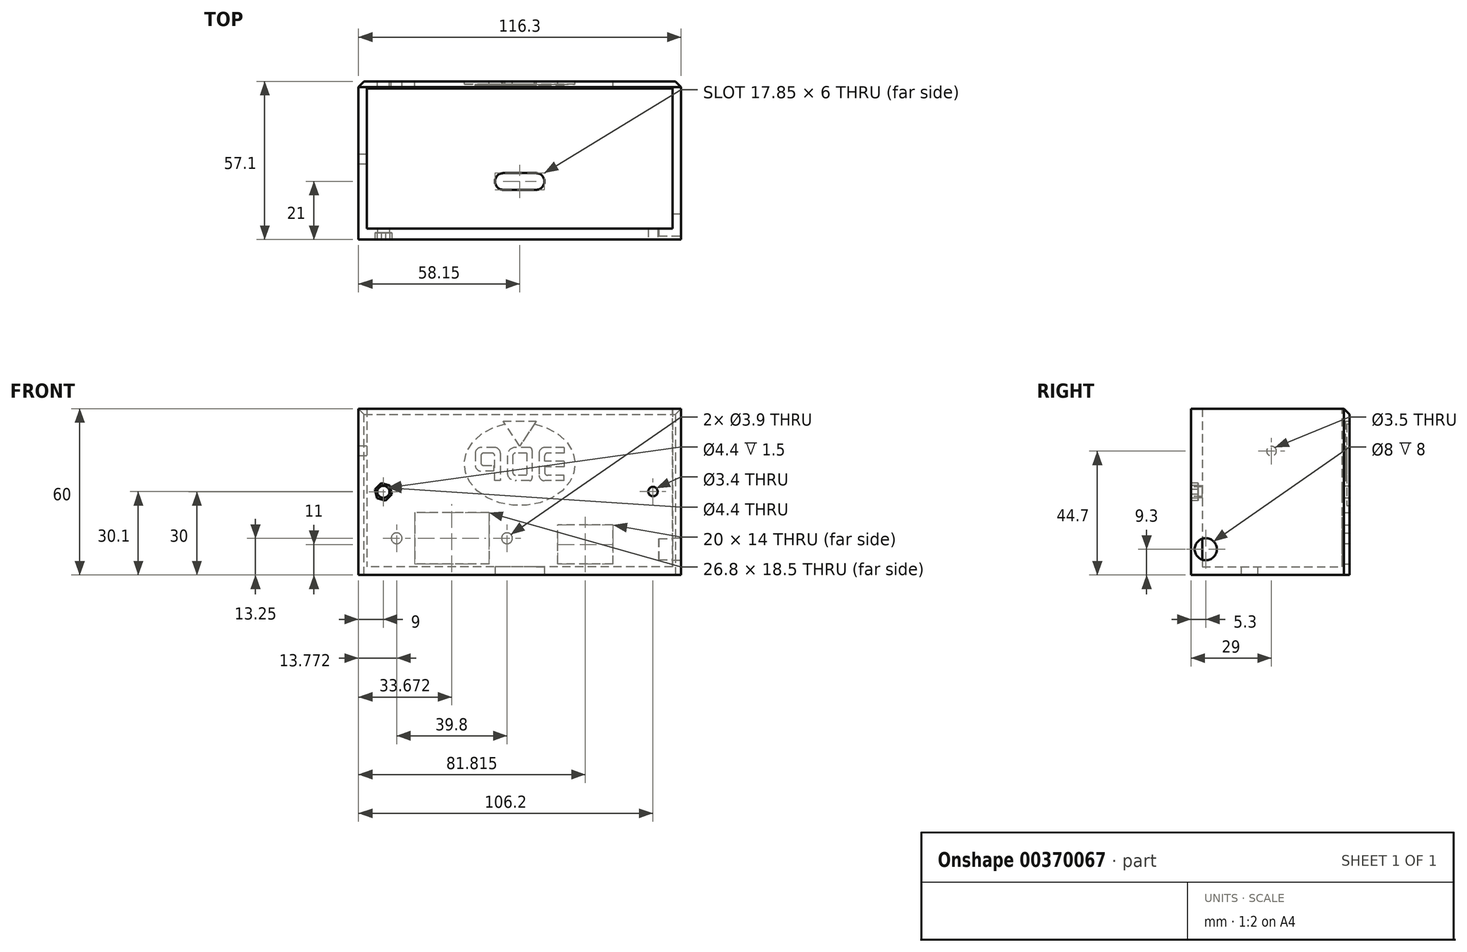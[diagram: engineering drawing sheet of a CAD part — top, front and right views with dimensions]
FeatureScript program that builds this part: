
annotation { "Feature Type Name" : "Feature", "Feature Type Description" : "" }
export const myFeature = defineFeature(function(context is Context, id is Id, definition is map)
    precondition{}
    {
        {
            var Q0;
            Q0=qCreatedBy(makeId("Front.planeOp"),FACE);
            var sketch = newSketch(context, id + "F0", { "sketchPlane" : qUnion([Q0])});
            skLineSegment(sketch, "E0.bottom", {"start": v(0, 0) * mm, "end": v(116.3, 0) * mm});
            skLineSegment(sketch, "E0.top", {"start": v(0, 70) * mm, "end": v(116.3, 70) * mm});
            skLineSegment(sketch, "E0.left", {"start": v(0, 0) * mm, "end": v(0, 70) * mm});
            skLineSegment(sketch, "E0.right", {"start": v(116.3, 0) * mm, "end": v(116.3, 70) * mm});
            skCircle(sketch, "E1", {"center": v(18, 61.5) * mm, "radius": 1.7 * mm});
            skCircle(sketch, "E2", {"center": v(103.3, 61.5) * mm, "radius": 1.7 * mm});
            skCircle(sketch, "E3", {"center": v(106.2, 5.1) * mm, "radius": 1.7 * mm});
            skCircle(sketch, "E4", {"center": v(9, 5) * mm, "radius": 2.2 * mm});
            skLineSegment(sketch, "E5.top", {"start": v(116.3, 0) * mm, "end": v(119.3, 0) * mm});
            skPoint(sketch, "E6.orphan", {"position": v(-3, 70) * mm});
            skPoint(sketch, "E7.right.end.orphan", {"position": v(-3, 35) * mm});
            skPoint(sketch, "E8.right.end.orphan", {"position": v(119.3, 35) * mm});
            skPoint(sketch, "E5.bottom.end.orphan", {"position": v(119.3, 70) * mm});
            skPoint(sketch, "E9.top.end.orphan", {"position": v(-3, 0) * mm});
            skSolve(sketch);
        }
        {
            var Q0;
            Q0=makeQuery(id+"F0.imprint","IMPRINT",FACE,{"disambiguationData":[TD([[makeQuery(id+"F0.imprint","IMPRINT",EDGE,{"derivedFrom":sQuery(id+"F0.wireOp",EDGE,"E0.bottom")}),1.0]])]});
            extrude(context, id + "F1", {"entities" : qUnion([Q0]), "oppositeDirection" : true, "depth" : 4 * mm});
        }
        {
            var Q0;
            Q0=makeQuery(id+"F1.opExtrude","CAP_FACE",FACE,{"disambiguationData":[OSD([sQuery(id+"F0.wireOp",EDGE,"E0.bottom"),sQuery(id+"F0.wireOp",EDGE,"E0.top"),sQuery(id+"F0.wireOp",EDGE,"E0.left"),sQuery(id+"F0.wireOp",EDGE,"E0.right"),sQuery(id+"F0.wireOp",EDGE,"E1"),sQuery(id+"F0.wireOp",EDGE,"E2"),sQuery(id+"F0.wireOp",EDGE,"E3"),sQuery(id+"F0.wireOp",EDGE,"E4")])],"isStart":false});
            var sketch = newSketch(context, id + "F2", { "sketchPlane" : qUnion([Q0])});
            skPoint(sketch, "E10.oppositeSnap0", {"position": v(-116.3, 35) * mm});
            skLineSegment(sketch, "E10.top", {"start": v(-116.3, 35) * mm, "end": v(-113.3, 35) * mm});
            skLineSegment(sketch, "E10.left", {"start": v(-116.3, 0) * mm, "end": v(-116.3, 35) * mm});
            skLineSegment(sketch, "E10.right", {"start": v(-113.3, 0) * mm, "end": v(-113.3, 35) * mm});
            skPoint(sketch, "E11.oppositeSnap0", {"position": v(0, 35) * mm});
            skLineSegment(sketch, "E11.top", {"start": v(0, 35) * mm, "end": v(-3, 35) * mm});
            skLineSegment(sketch, "E11.left", {"start": v(0, 0) * mm, "end": v(0, 35) * mm});
            skLineSegment(sketch, "E11.right", {"start": v(-3, 0) * mm, "end": v(-3, 35) * mm});
            skLineSegment(sketch, "E12.top", {"start": v(-116.3, -25) * mm, "end": v(-113.3, -25) * mm});
            skLineSegment(sketch, "E12.left", {"start": v(-116.3, 0) * mm, "end": v(-116.3, -25) * mm});
            skLineSegment(sketch, "E12.right", {"start": v(-113.3, 0) * mm, "end": v(-113.3, -25) * mm});
            skLineSegment(sketch, "E13.top", {"start": v(0, -25) * mm, "end": v(-3, -25) * mm});
            skLineSegment(sketch, "E13.left", {"start": v(0, 0) * mm, "end": v(0, -25) * mm});
            skLineSegment(sketch, "E13.right", {"start": v(-3, 0) * mm, "end": v(-3, -25) * mm});
            skSolve(sketch);
        }
        {
            var Q0;
            Q0 = qSketchRegion(id + "F2", true);
            extrude(context, id + "F3", {"entities" : qUnion([Q0]), "operationType" : NewBodyOperationType.ADD, "depth" : 53.1 * mm});
        }
        {
            var Q0;
            Q0=makeQuery(id+"F3.boolean.opBoolean","MERGE",FACE,{"derivedFrom":[makeQuery(id+"F1.opExtrude","SWEPT_FACE",FACE,{"disambiguationData":[OSD([sQuery(id+"F0.wireOp",EDGE,"E0.left")])]}),makeQuery(id+"F3.opExtrude","SWEPT_FACE",FACE,{"disambiguationData":[OSD([sQuery(id+"F2.wireOp",EDGE,"E11.left"),sQuery(id+"F2.wireOp",EDGE,"E13.left")])]})]});
            var sketch = newSketch(context, id + "F4", { "sketchPlane" : qUnion([Q0])});
            skLineSegment(sketch, "E14", {"start": v(-57.1, 35) * mm, "end": v(-57.1, -25) * mm});
            skLineSegment(sketch, "E15", {"start": v(-57.1, -25) * mm, "end": v(0, -25) * mm});
            skLineSegment(sketch, "E16", {"start": v(0, -25) * mm, "end": v(0, 0) * mm});
            skLineSegment(sketch, "E17", {"start": v(0, 0) * mm, "end": v(-4, 0) * mm});
            skLineSegment(sketch, "E18", {"start": v(-4, 0) * mm, "end": v(-4, -22) * mm});
            skLineSegment(sketch, "E19", {"start": v(-4, -22) * mm, "end": v(-54.5, -22) * mm});
            skLineSegment(sketch, "E20", {"start": v(-54.5, -22) * mm, "end": v(-54.5, 35) * mm});
            skLineSegment(sketch, "E21", {"start": v(-54.5, 35) * mm, "end": v(-57.1, 35) * mm});
            skSolve(sketch);
        }
        {
            var Q0;
            Q0 = qSketchRegion(id + "F4", true);
            extrude(context, id + "F5", {"entities" : qUnion([Q0]), "operationType" : NewBodyOperationType.ADD, "oppositeDirection" : true, "depth" : 116.3 * mm});
        }
        {
            var Q0;
            Q0=makeQuery(id+"F5.boolean.opBoolean","MERGE",FACE,{"derivedFrom":[makeQuery(id+"F3.opExtrude","CAP_FACE",FACE,{"disambiguationData":[OSD([sQuery(id+"F2.wireOp",EDGE,"E10.top"),sQuery(id+"F2.wireOp",EDGE,"E10.left"),sQuery(id+"F2.wireOp",EDGE,"E10.right"),sQuery(id+"F2.wireOp",EDGE,"E12.top"),sQuery(id+"F2.wireOp",EDGE,"E12.left"),sQuery(id+"F2.wireOp",EDGE,"E12.right")])],"isStart":false}),makeQuery(id+"F3.opExtrude","CAP_FACE",FACE,{"disambiguationData":[OSD([sQuery(id+"F2.wireOp",EDGE,"E11.top"),sQuery(id+"F2.wireOp",EDGE,"E11.left"),sQuery(id+"F2.wireOp",EDGE,"E11.right"),sQuery(id+"F2.wireOp",EDGE,"E13.top"),sQuery(id+"F2.wireOp",EDGE,"E13.left"),sQuery(id+"F2.wireOp",EDGE,"E13.right")])],"isStart":false}),makeQuery(id+"F5.opExtrude","SWEPT_FACE",FACE,{"disambiguationData":[OSD([sQuery(id+"F4.wireOp",EDGE,"E14")])]})]});
            var sketch = newSketch(context, id + "F6", { "sketchPlane" : qUnion([Q0])});
            skLineSegment(sketch, "E22.bottom", {"start": v(-47.07, -2.5) * mm, "end": v(-20.27, -2.5) * mm});
            skLineSegment(sketch, "E22.top", {"start": v(-47.07, -21) * mm, "end": v(-20.27, -21) * mm});
            skLineSegment(sketch, "E22.left", {"start": v(-47.07, -2.5) * mm, "end": v(-47.07, -21) * mm});
            skLineSegment(sketch, "E22.right", {"start": v(-20.27, -2.5) * mm, "end": v(-20.27, -21) * mm});
            skPoint(sketch, "E23.right.end.orphan", {"position": v(-79.44, -21) * mm});
            skLineSegment(sketch, "E24", {"start": v(-20.27, -11.75) * mm, "end": v(-13.77, -11.75) * mm});
            skCircle(sketch, "E25", {"center": v(-13.77, -11.75) * mm, "radius": 1.95 * mm});
            skLineSegment(sketch, "E26", {"start": v(-33.67, -2.5) * mm, "end": v(-33.67, -21) * mm, "construction": true});
            skCircle(sketch, "E27.MirrorC", {"center": v(-53.57, -11.75) * mm, "radius": 1.95 * mm});
            skLineSegment(sketch, "E28.bottom", {"start": v(-91.81, -21) * mm, "end": v(-71.81, -21) * mm});
            skLineSegment(sketch, "E28.top", {"start": v(-91.81, -7) * mm, "end": v(-71.81, -7) * mm});
            skLineSegment(sketch, "E28.left", {"start": v(-91.81, -21) * mm, "end": v(-91.81, -7) * mm});
            skLineSegment(sketch, "E28.right", {"start": v(-71.81, -21) * mm, "end": v(-71.81, -7) * mm});
            skSolve(sketch);
        }
        {
            var Q0;
            Q0 = qSketchRegion(id + "F6", true);
            extrude(context, id + "F7", {"entities" : qUnion([Q0]), "operationType" : NewBodyOperationType.REMOVE, "oppositeDirection" : true, "depth" : 25 * mm});
        }
        {
            var Q0;
            Q0=makeQuery(id+"F5.boolean.opBoolean","MERGE",FACE,{"derivedFrom":[makeQuery(id+"F3.boolean.opBoolean","MERGE",FACE,{"derivedFrom":[makeQuery(id+"F1.opExtrude","SWEPT_FACE",FACE,{"disambiguationData":[OSD([sQuery(id+"F0.wireOp",EDGE,"E0.left")])]}),makeQuery(id+"F3.opExtrude","SWEPT_FACE",FACE,{"disambiguationData":[OSD([sQuery(id+"F2.wireOp",EDGE,"E11.left"),sQuery(id+"F2.wireOp",EDGE,"E13.left")])]})]}),makeQuery(id+"F5.opExtrude","CAP_FACE",FACE,{"disambiguationData":[OSD([sQuery(id+"F4.wireOp",EDGE,"E14"),sQuery(id+"F4.wireOp",EDGE,"E15"),sQuery(id+"F4.wireOp",EDGE,"E16"),sQuery(id+"F4.wireOp",EDGE,"E17"),sQuery(id+"F4.wireOp",EDGE,"E18"),sQuery(id+"F4.wireOp",EDGE,"E19"),sQuery(id+"F4.wireOp",EDGE,"E20"),sQuery(id+"F4.wireOp",EDGE,"E21")])],"isStart":true})]});
            var sketch = newSketch(context, id + "F8", { "sketchPlane" : qUnion([Q0])});
            skLineSegment(sketch, "E29", {"start": v(0, 0) * mm, "end": v(-29, 0) * mm, "construction": true});
            skLineSegment(sketch, "E30", {"start": v(-29, 0) * mm, "end": v(-29, 19.7) * mm, "construction": true});
            skCircle(sketch, "E31", {"center": v(-29, 19.7) * mm, "radius": 1.75 * mm});
            skLineSegment(sketch, "E32", {"start": v(-4, 70) * mm, "end": v(0, 70) * mm});
            skSolve(sketch);
        }
        {
            var Q0;
            Q0=makeQuery(id+"F8.imprint","IMPRINT",FACE,{"disambiguationData":[TD([[makeQuery(id+"F8.imprint","IMPRINT",EDGE,{"derivedFrom":sQuery(id+"F8.wireOp",EDGE,"E31")}),1.0]])]});
            extrude(context, id + "F9", {"entities" : qUnion([Q0]), "operationType" : NewBodyOperationType.REMOVE, "oppositeDirection" : true, "depth" : 25 * mm});
        }
        {
            var Q0;
            Q0=makeQuery(id+"F5.boolean.opBoolean","MERGE",FACE,{"derivedFrom":[makeQuery(id+"F1.opExtrude","CAP_FACE",FACE,{"disambiguationData":[OSD([sQuery(id+"F0.wireOp",EDGE,"E0.bottom"),sQuery(id+"F0.wireOp",EDGE,"E0.top"),sQuery(id+"F0.wireOp",EDGE,"E0.left"),sQuery(id+"F0.wireOp",EDGE,"E0.right"),sQuery(id+"F0.wireOp",EDGE,"E1"),sQuery(id+"F0.wireOp",EDGE,"E2"),sQuery(id+"F0.wireOp",EDGE,"E3"),sQuery(id+"F0.wireOp",EDGE,"E4")])],"isStart":false}),makeQuery(id+"F5.opExtrude","SWEPT_FACE",FACE,{"disambiguationData":[OSD([sQuery(id+"F4.wireOp",EDGE,"E18")])]})]});
            var sketch = newSketch(context, id + "F10", { "sketchPlane" : qUnion([Q0])});
            skLineSegment(sketch, "E33.bottom", {"start": v(-116.3, 70) * mm, "end": v(0, 70) * mm});
            skLineSegment(sketch, "E33.top", {"start": v(-116.3, 35) * mm, "end": v(0, 35) * mm});
            skLineSegment(sketch, "E33.left", {"start": v(-116.3, 70) * mm, "end": v(-116.3, 35) * mm});
            skLineSegment(sketch, "E33.right", {"start": v(0, 70) * mm, "end": v(0, 35) * mm});
            skSolve(sketch);
        }
        {
            var Q0;
            Q0 = qSketchRegion(id + "F10", true);
            extrude(context, id + "F11", {"entities" : qUnion([Q0]), "operationType" : NewBodyOperationType.REMOVE, "oppositeDirection" : true, "depth" : 25 * mm});
        }
        {
            var Q0;
            Q0=makeQuery(id+"F5.boolean.opBoolean","MERGE",FACE,{"derivedFrom":[makeQuery(id+"F3.opExtrude","CAP_FACE",FACE,{"disambiguationData":[OSD([sQuery(id+"F2.wireOp",EDGE,"E10.top"),sQuery(id+"F2.wireOp",EDGE,"E10.left"),sQuery(id+"F2.wireOp",EDGE,"E10.right"),sQuery(id+"F2.wireOp",EDGE,"E12.top"),sQuery(id+"F2.wireOp",EDGE,"E12.left"),sQuery(id+"F2.wireOp",EDGE,"E12.right")])],"isStart":false}),makeQuery(id+"F3.opExtrude","CAP_FACE",FACE,{"disambiguationData":[OSD([sQuery(id+"F2.wireOp",EDGE,"E11.top"),sQuery(id+"F2.wireOp",EDGE,"E11.left"),sQuery(id+"F2.wireOp",EDGE,"E11.right"),sQuery(id+"F2.wireOp",EDGE,"E13.top"),sQuery(id+"F2.wireOp",EDGE,"E13.left"),sQuery(id+"F2.wireOp",EDGE,"E13.right")])],"isStart":false}),makeQuery(id+"F5.opExtrude","SWEPT_FACE",FACE,{"disambiguationData":[OSD([sQuery(id+"F4.wireOp",EDGE,"E14")])]})]});
            var sketch = newSketch(context, id + "F12", { "sketchPlane" : qUnion([Q0])});
            skLineSegment(sketch, "E34", {"start": v(-78.15, 15) * mm, "end": v(-38.15, 15) * mm, "construction": true});
            skEllipticalArc(sketch, "E35", {});
            skPoint(sketch, "E36.orphan", {"position": v(-78.15, 30) * mm});
            skPoint(sketch, "E37.orphan", {"position": v(-38.15, 30) * mm});
            skPoint(sketch, "E38.orphan", {"position": v(-38.15, 0) * mm});
            skPoint(sketch, "E39.top.start.orphan", {"position": v(-78.15, 0) * mm});
            skLineSegment(sketch, "E40.bottom", {"start": v(-74.15, 21) * mm, "end": v(-67.15, 21) * mm});
            skLineSegment(sketch, "E40.top", {"start": v(-74.15, 9) * mm, "end": v(-67.15, 9) * mm});
            skLineSegment(sketch, "E40.right", {"start": v(-65.15, 19) * mm, "end": v(-65.15, 11) * mm});
            skLineSegment(sketch, "E41.bottom", {"start": v(-61.65, 21) * mm, "end": v(-56.65, 21) * mm});
            skLineSegment(sketch, "E41.top", {"start": v(-61.65, 9) * mm, "end": v(-56.65, 9) * mm});
            skLineSegment(sketch, "E41.left", {"start": v(-62.65, 20) * mm, "end": v(-62.65, 10) * mm});
            skLineSegment(sketch, "E41.right", {"start": v(-53.65, 18) * mm, "end": v(-53.65, 12) * mm});
            skLineSegment(sketch, "E42.bottom", {"start": v(-49.15, 21) * mm, "end": v(-44.15, 21) * mm});
            skLineSegment(sketch, "E42.left", {"start": v(-51.15, 19) * mm, "end": v(-51.15, 9) * mm});
            skLineSegment(sketch, "E42.right", {"start": v(-42.15, 19) * mm, "end": v(-42.15, 14.5) * mm});
            skPoint(sketch, "E43.visualSharp", {"position": v(-65.15, 21) * mm});
            skArc(sketch, "E43.filletArc", {"start": v(-65.15, 19) * mm, "mid": v(-65.74, 20.41) * mm, "end": v(-67.15, 21) * mm});
            skPoint(sketch, "E44.visualSharp", {"position": v(-65.15, 9) * mm});
            skArc(sketch, "E44.filletArc", {"start": v(-67.15, 9) * mm, "mid": v(-65.74, 9.59) * mm, "end": v(-65.15, 11) * mm});
            skPoint(sketch, "E45.visualSharp", {"position": v(-53.65, 21) * mm});
            skArc(sketch, "E45.filletArc", {"start": v(-53.65, 18) * mm, "mid": v(-54.53, 20.12) * mm, "end": v(-56.65, 21) * mm});
            skPoint(sketch, "E46.visualSharp", {"position": v(-53.65, 9) * mm});
            skArc(sketch, "E46.filletArc", {"start": v(-56.65, 9) * mm, "mid": v(-54.53, 9.88) * mm, "end": v(-53.65, 12) * mm});
            skPoint(sketch, "E47.visualSharp", {"position": v(-51.15, 21) * mm});
            skArc(sketch, "E47.filletArc", {"start": v(-49.15, 21) * mm, "mid": v(-50.56, 20.41) * mm, "end": v(-51.15, 19) * mm});
            skPoint(sketch, "E48.visualSharp", {"position": v(-42.15, 21) * mm});
            skArc(sketch, "E48.filletArc", {"start": v(-42.15, 19) * mm, "mid": v(-42.74, 20.41) * mm, "end": v(-44.15, 21) * mm});
            skPoint(sketch, "E49.visualSharp", {"position": v(-62.65, 21) * mm});
            skArc(sketch, "E49.filletArc", {"start": v(-61.65, 21) * mm, "mid": v(-62.36, 20.7) * mm, "end": v(-62.65, 20) * mm});
            skPoint(sketch, "E50.visualSharp", {"position": v(-62.65, 9) * mm});
            skArc(sketch, "E50.filletArc", {"start": v(-62.65, 10) * mm, "mid": v(-62.36, 9.3) * mm, "end": v(-61.65, 9) * mm});
            skLineSegment(sketch, "E51.0", {"start": v(-60.65, 19) * mm, "end": v(-56.65, 19) * mm});
            skLineSegment(sketch, "E51.1", {"start": v(-60.65, 11) * mm, "end": v(-56.65, 11) * mm});
            skArc(sketch, "E51.2", {"start": v(-56.65, 11) * mm, "mid": v(-55.94, 11.3) * mm, "end": v(-55.65, 12) * mm});
            skLineSegment(sketch, "E51.3", {"start": v(-60.65, 19) * mm, "end": v(-60.65, 11) * mm});
            skLineSegment(sketch, "E51.4", {"start": v(-55.65, 18) * mm, "end": v(-55.65, 12) * mm});
            skArc(sketch, "E51.5", {"start": v(-55.65, 18) * mm, "mid": v(-55.94, 18.7) * mm, "end": v(-56.65, 19) * mm});
            skLineSegment(sketch, "E52", {"start": v(-74.15, 21) * mm, "end": v(-74.15, 19) * mm});
            skLineSegment(sketch, "E53", {"start": v(-74.15, 9) * mm, "end": v(-74.15, 11) * mm});
            skLineSegment(sketch, "E54", {"start": v(-74.15, 19) * mm, "end": v(-68.15, 19) * mm});
            skLineSegment(sketch, "E55", {"start": v(-67.15, 16) * mm, "end": v(-67.15, 18) * mm});
            skLineSegment(sketch, "E56", {"start": v(-74.15, 16) * mm, "end": v(-67.15, 16) * mm});
            skLineSegment(sketch, "E57", {"start": v(-74.15, 14) * mm, "end": v(-67.15, 14) * mm});
            skLineSegment(sketch, "E58", {"start": v(-67.15, 14) * mm, "end": v(-67.15, 12) * mm});
            skLineSegment(sketch, "E59", {"start": v(-74.15, 11) * mm, "end": v(-68.15, 11) * mm});
            skArc(sketch, "E60.filletArc", {"start": v(-68.15, 11) * mm, "mid": v(-67.44, 11.3) * mm, "end": v(-67.15, 12) * mm});
            skArc(sketch, "E61.filletArc", {"start": v(-67.15, 18) * mm, "mid": v(-67.44, 18.7) * mm, "end": v(-68.15, 19) * mm});
            skLineSegment(sketch, "E62", {"start": v(-51.15, 9) * mm, "end": v(-49.15, 9) * mm});
            skLineSegment(sketch, "E63", {"start": v(-49.15, 9) * mm, "end": v(-49.15, 18) * mm});
            skLineSegment(sketch, "E64", {"start": v(-44.15, 18) * mm, "end": v(-44.15, 15.5) * mm});
            skLineSegment(sketch, "E65", {"start": v(-45.15, 14.5) * mm, "end": v(-47.96, 14.5) * mm});
            skLineSegment(sketch, "E66", {"start": v(-47.88, 12.5) * mm, "end": v(-44.15, 12.5) * mm});
            skPoint(sketch, "E67.orphan", {"position": v(-42.15, 9) * mm});
            skLineSegment(sketch, "E68", {"start": v(-48.15, 19) * mm, "end": v(-45.15, 19) * mm});
            skPoint(sketch, "E69.visualSharp", {"position": v(-42.15, 12.5) * mm});
            skArc(sketch, "E69.filletArc", {"start": v(-44.15, 12.5) * mm, "mid": v(-42.74, 13.08) * mm, "end": v(-42.15, 14.5) * mm});
            skArc(sketch, "E70.filletArc", {"start": v(-45.15, 14.5) * mm, "mid": v(-44.44, 14.79) * mm, "end": v(-44.15, 15.5) * mm});
            skArc(sketch, "E71.filletArc", {"start": v(-44.15, 18) * mm, "mid": v(-44.44, 18.7) * mm, "end": v(-45.15, 19) * mm});
            skArc(sketch, "E72.filletArc", {"start": v(-48.15, 19) * mm, "mid": v(-48.86, 18.7) * mm, "end": v(-49.15, 18) * mm});
            skLineSegment(sketch, "E73", {"start": v(-47.96, 14.5) * mm, "end": v(-48.76, 14.5) * mm});
            skLineSegment(sketch, "E74", {"start": v(-48.76, 14.5) * mm, "end": v(-48.76, 12.5) * mm});
            skLineSegment(sketch, "E75", {"start": v(-48.76, 12.5) * mm, "end": v(-47.88, 12.5) * mm});
            skLineSegment(sketch, "E76.trimOffspring", {"start": v(-58.15, 11) * mm, "end": v(-58.15, 0) * mm, "construction": true});
            skLineSegment(sketch, "E77.trimOffspring", {"start": v(-58.15, 21) * mm, "end": v(-58.15, 19) * mm, "construction": true});
            skPoint(sketch, "E78.start.orphan", {"position": v(-58.15, 30) * mm});
            skPoint(sketch, "E79.orphan", {"position": v(-58.15, 27) * mm});
            skLineSegment(sketch, "E80", {"start": v(-58.15, 30.5) * mm, "end": v(-64.15, 30.5) * mm});
            skLineSegment(sketch, "E81", {"start": v(-64.15, 30.5) * mm, "end": v(-58.15, 21.5) * mm});
            skLineSegment(sketch, "E82", {"start": v(-58.15, 30.5) * mm, "end": v(-52.15, 30.5) * mm});
            skLineSegment(sketch, "E83", {"start": v(-58.15, 21.5) * mm, "end": v(-52.15, 30.5) * mm});
            skLineSegment(sketch, "E84", {"start": v(-74.15, 16) * mm, "end": v(-74.15, 14) * mm});
            const initialGuessF12  = {"E35": [-0.05815, 0.015, -1, 0, 0.02, 0.015, 4.981010063502463, 4.443767897266916]};
            skSetInitialGuess(sketch, initialGuessF12);
            skSolve(sketch);
        }
        {
            var Q0;
            Q0=makeQuery(id+"F12.imprint","IMPRINT",FACE,{"disambiguationData":[TD([[makeQuery(id+"F12.imprint","IMPRINT",EDGE,{"derivedFrom":sQuery(id+"F12.wireOp",EDGE,"E40.bottom")}),-1.0]])]});
            var Q1;
            Q1=makeQuery(id+"F12.imprint","IMPRINT",FACE,{"disambiguationData":[TD([[makeQuery(id+"F12.imprint","IMPRINT",EDGE,{"derivedFrom":sQuery(id+"F12.wireOp",EDGE,"E41.bottom")}),-1.0]])]});
            var Q2;
            Q2=makeQuery(id+"F12.imprint","IMPRINT",FACE,{"disambiguationData":[TD([[makeQuery(id+"F12.imprint","IMPRINT",EDGE,{"derivedFrom":sQuery(id+"F12.wireOp",EDGE,"E42.bottom")}),-1.0]])]});
            extrude(context, id + "F13", {"entities" : qUnion([Q0, Q1, Q2]), "operationType" : NewBodyOperationType.REMOVE, "oppositeDirection" : true, "depth" : 1.5 * mm});
        }
        {
            var Q0;
            {var subQ7=sQuery(id+"F4.wireOp",EDGE,"E14");var subQ8=sQuery(id+"F2.wireOp",EDGE,"E12.top");var subQ9=sQuery(id+"F2.wireOp",EDGE,"E13.left");var subQ10=sQuery(id+"F2.wireOp",EDGE,"E11.left");var subQ11=sQuery(id+"F2.wireOp",EDGE,"E11.top");var subQ12=sQuery(id+"F2.wireOp",EDGE,"E13.top");var subQ13=sQuery(id+"F2.wireOp",EDGE,"E10.top");var subQ14=sQuery(id+"F2.wireOp",EDGE,"E12.left");var subQ15=sQuery(id+"F2.wireOp",EDGE,"E10.left");Q0=makeQuery(id+"F13.boolean.opBoolean","SPLIT",FACE,{"disambiguationData":[TD([makeQuery(id+"F1.opExtrude","SWEPT_FACE",FACE,{"disambiguationData":[OSD([sQuery(id+"F0.wireOp",EDGE,"E0.left")])]})])],"derivedFrom":makeQuery(id+"F5.boolean.opBoolean","MERGE",FACE,{"derivedFrom":[makeQuery(id+"F3.opExtrude","CAP_FACE",FACE,{"disambiguationData":[OSD([subQ13,subQ15,sQuery(id+"F2.wireOp",EDGE,"E10.right"),subQ8,subQ14,sQuery(id+"F2.wireOp",EDGE,"E12.right")])],"isStart":false}),makeQuery(id+"F3.opExtrude","CAP_FACE",FACE,{"disambiguationData":[OSD([subQ11,subQ10,sQuery(id+"F2.wireOp",EDGE,"E11.right"),subQ12,subQ9,sQuery(id+"F2.wireOp",EDGE,"E13.right")])],"isStart":false}),makeQuery(id+"F5.opExtrude","SWEPT_FACE",FACE,{"disambiguationData":[OSD([subQ7])]})]})});}
            var sketch = newSketch(context, id + "F14", { "sketchPlane" : qUnion([Q0])});
            skEllipticalArc(sketch, "E85.1", {});
            skPoint(sketch, "E85.2", {"position": v(-78.15, 30) * mm});
            skPoint(sketch, "E85.3", {"position": v(-38.15, 30) * mm});
            skPoint(sketch, "E85.4", {"position": v(-38.15, 0) * mm});
            skPoint(sketch, "E85.5", {"position": v(-78.15, 0) * mm});
            skLineSegment(sketch, "E85.6", {"start": v(-74.15, 21) * mm, "end": v(-67.15, 21) * mm});
            skLineSegment(sketch, "E85.7", {"start": v(-74.15, 9) * mm, "end": v(-67.15, 9) * mm});
            skLineSegment(sketch, "E85.8", {"start": v(-65.15, 19) * mm, "end": v(-65.15, 11) * mm});
            skLineSegment(sketch, "E85.9", {"start": v(-61.65, 21) * mm, "end": v(-56.65, 21) * mm});
            skLineSegment(sketch, "E85.10", {"start": v(-61.65, 9) * mm, "end": v(-56.65, 9) * mm});
            skLineSegment(sketch, "E85.11", {"start": v(-62.65, 20) * mm, "end": v(-62.65, 10) * mm});
            skLineSegment(sketch, "E85.12", {"start": v(-53.65, 18) * mm, "end": v(-53.65, 12) * mm});
            skLineSegment(sketch, "E85.13", {"start": v(-49.15, 21) * mm, "end": v(-44.15, 21) * mm});
            skLineSegment(sketch, "E85.14", {"start": v(-51.15, 19) * mm, "end": v(-51.15, 9) * mm});
            skLineSegment(sketch, "E85.15", {"start": v(-42.15, 19) * mm, "end": v(-42.15, 14.5) * mm});
            skPoint(sketch, "E85.16", {"position": v(-65.15, 21) * mm});
            skArc(sketch, "E85.17", {"start": v(-65.15, 19) * mm, "mid": v(-65.74, 20.41) * mm, "end": v(-67.15, 21) * mm});
            skPoint(sketch, "E85.18", {"position": v(-65.15, 9) * mm});
            skArc(sketch, "E85.19", {"start": v(-67.15, 9) * mm, "mid": v(-65.74, 9.59) * mm, "end": v(-65.15, 11) * mm});
            skPoint(sketch, "E85.20", {"position": v(-53.65, 21) * mm});
            skArc(sketch, "E85.21", {"start": v(-53.65, 18) * mm, "mid": v(-54.53, 20.12) * mm, "end": v(-56.65, 21) * mm});
            skPoint(sketch, "E85.22", {"position": v(-53.65, 9) * mm});
            skArc(sketch, "E85.23", {"start": v(-56.65, 9) * mm, "mid": v(-54.53, 9.88) * mm, "end": v(-53.65, 12) * mm});
            skPoint(sketch, "E85.24", {"position": v(-51.15, 21) * mm});
            skArc(sketch, "E85.25", {"start": v(-49.15, 21) * mm, "mid": v(-50.56, 20.41) * mm, "end": v(-51.15, 19) * mm});
            skPoint(sketch, "E85.26", {"position": v(-42.15, 21) * mm});
            skArc(sketch, "E85.27", {"start": v(-42.15, 19) * mm, "mid": v(-42.74, 20.41) * mm, "end": v(-44.15, 21) * mm});
            skPoint(sketch, "E85.28", {"position": v(-62.65, 21) * mm});
            skArc(sketch, "E85.29", {"start": v(-61.65, 21) * mm, "mid": v(-62.36, 20.7) * mm, "end": v(-62.65, 20) * mm});
            skPoint(sketch, "E85.30", {"position": v(-62.65, 9) * mm});
            skArc(sketch, "E85.31", {"start": v(-62.65, 10) * mm, "mid": v(-62.36, 9.3) * mm, "end": v(-61.65, 9) * mm});
            skLineSegment(sketch, "E85.33", {"start": v(-60.65, 11) * mm, "end": v(-56.65, 11) * mm});
            skArc(sketch, "E85.34", {"start": v(-56.65, 11) * mm, "mid": v(-55.94, 11.3) * mm, "end": v(-55.65, 12) * mm});
            skLineSegment(sketch, "E85.35", {"start": v(-60.65, 15) * mm, "end": v(-60.65, 11) * mm});
            skLineSegment(sketch, "E85.36", {"start": v(-55.65, 18) * mm, "end": v(-55.65, 12) * mm});
            skArc(sketch, "E85.37", {"start": v(-55.65, 18) * mm, "mid": v(-55.94, 18.7) * mm, "end": v(-56.65, 19) * mm});
            skLineSegment(sketch, "E85.38", {"start": v(-74.15, 21) * mm, "end": v(-74.15, 19) * mm});
            skLineSegment(sketch, "E85.39", {"start": v(-74.15, 9) * mm, "end": v(-74.15, 11) * mm});
            skLineSegment(sketch, "E85.40", {"start": v(-74.15, 19) * mm, "end": v(-68.15, 19) * mm});
            skLineSegment(sketch, "E85.41", {"start": v(-67.15, 16) * mm, "end": v(-67.15, 18) * mm});
            skLineSegment(sketch, "E85.42", {"start": v(-74.15, 16) * mm, "end": v(-67.15, 16) * mm});
            skLineSegment(sketch, "E85.43", {"start": v(-74.15, 14) * mm, "end": v(-67.15, 14) * mm});
            skLineSegment(sketch, "E85.44", {"start": v(-67.15, 14) * mm, "end": v(-67.15, 12) * mm});
            skLineSegment(sketch, "E85.45", {"start": v(-74.15, 11) * mm, "end": v(-68.15, 11) * mm});
            skPoint(sketch, "E85.46", {"position": v(-67.15, 11) * mm});
            skArc(sketch, "E85.47", {"start": v(-68.15, 11) * mm, "mid": v(-67.44, 11.3) * mm, "end": v(-67.15, 12) * mm});
            skPoint(sketch, "E85.48", {"position": v(-67.15, 19) * mm});
            skArc(sketch, "E85.49", {"start": v(-67.15, 18) * mm, "mid": v(-67.44, 18.7) * mm, "end": v(-68.15, 19) * mm});
            skLineSegment(sketch, "E85.50", {"start": v(-51.15, 9) * mm, "end": v(-49.15, 9) * mm});
            skLineSegment(sketch, "E85.51", {"start": v(-49.15, 9) * mm, "end": v(-49.15, 18) * mm});
            skLineSegment(sketch, "E85.52", {"start": v(-44.15, 18) * mm, "end": v(-44.15, 15.5) * mm});
            skLineSegment(sketch, "E85.53", {"start": v(-45.15, 14.5) * mm, "end": v(-47.96, 14.5) * mm});
            skLineSegment(sketch, "E85.54", {"start": v(-47.88, 12.5) * mm, "end": v(-44.15, 12.5) * mm});
            skPoint(sketch, "E85.55", {"position": v(-42.15, 9) * mm});
            skLineSegment(sketch, "E85.56", {"start": v(-48.15, 19) * mm, "end": v(-45.15, 19) * mm});
            skPoint(sketch, "E85.57", {"position": v(-42.15, 12.5) * mm});
            skArc(sketch, "E85.58", {"start": v(-44.15, 12.5) * mm, "mid": v(-42.74, 13.08) * mm, "end": v(-42.15, 14.5) * mm});
            skPoint(sketch, "E85.59", {"position": v(-44.15, 14.5) * mm});
            skArc(sketch, "E85.60", {"start": v(-45.15, 14.5) * mm, "mid": v(-44.44, 14.79) * mm, "end": v(-44.15, 15.5) * mm});
            skPoint(sketch, "E85.61", {"position": v(-44.15, 19) * mm});
            skArc(sketch, "E85.62", {"start": v(-44.15, 18) * mm, "mid": v(-44.44, 18.7) * mm, "end": v(-45.15, 19) * mm});
            skPoint(sketch, "E85.63", {"position": v(-49.15, 19) * mm});
            skArc(sketch, "E85.64", {"start": v(-48.15, 19) * mm, "mid": v(-48.86, 18.7) * mm, "end": v(-49.15, 18) * mm});
            skLineSegment(sketch, "E85.65", {"start": v(-47.96, 14.5) * mm, "end": v(-48.76, 14.5) * mm});
            skLineSegment(sketch, "E85.66", {"start": v(-48.76, 14.5) * mm, "end": v(-48.76, 12.5) * mm});
            skLineSegment(sketch, "E85.67", {"start": v(-48.76, 12.5) * mm, "end": v(-47.88, 12.5) * mm});
            skPoint(sketch, "E85.70", {"position": v(-58.15, 30) * mm});
            skPoint(sketch, "E85.71", {"position": v(-58.15, 27) * mm});
            skLineSegment(sketch, "E85.72", {"start": v(-58.15, 30.5) * mm, "end": v(-64.15, 30.5) * mm});
            skLineSegment(sketch, "E85.73", {"start": v(-64.15, 30.5) * mm, "end": v(-58.15, 21.5) * mm});
            skLineSegment(sketch, "E85.74", {"start": v(-58.15, 30.5) * mm, "end": v(-52.15, 30.5) * mm});
            skLineSegment(sketch, "E85.75", {"start": v(-58.15, 21.5) * mm, "end": v(-52.15, 30.5) * mm});
            skLineSegment(sketch, "E85.76", {"start": v(-74.15, 16) * mm, "end": v(-74.15, 14) * mm});
            skPoint(sketch, "E85.69.end.orphan", {"position": v(-58.15, 19) * mm});
            skPoint(sketch, "E85.69.start.orphan", {"position": v(-58.15, 21) * mm});
            skPoint(sketch, "E86.orphan", {"position": v(-60.65, 19) * mm});
            skPoint(sketch, "E85.32.end.orphan", {"position": v(-56.65, 19) * mm});
            skPoint(sketch, "E87.orphan", {"position": v(-58.15, 0) * mm});
            skPoint(sketch, "E85.68.start.orphan", {"position": v(-58.15, 11) * mm});
            skPoint(sketch, "E88.trimOffspring.end.orphan", {"position": v(-38.15, 15) * mm});
            skPoint(sketch, "E85.0.start.orphan", {"position": v(-78.15, 15) * mm});
            const initialGuessF14  = {"E85.1": [-0.05815, 0.015, -1, 0, 0.02, 0.015, 4.981010063502463, 4.443767897266916]};
            skSetInitialGuess(sketch, initialGuessF14);
            skSolve(sketch);
        }
        {
            var Q0;
            {var subQ0=sQuery(id+"F14.wireOp",EDGE,"E85.1");Q0=makeQuery(id+"F14.imprint","IMPRINT",FACE,{"disambiguationData":[TD([[makeQuery(id+"F14.imprint","IMPRINT",EDGE,{"derivedFrom":subQ0}),1.0]])]});}
            extrude(context, id + "F15", {"entities" : qUnion([Q0]), "operationType" : NewBodyOperationType.REMOVE, "oppositeDirection" : true, "depth" : 1 * mm});
        }
        {
            var Q0;
            Q0=makeQuery(id+"F13.boolean.opBoolean","SPLIT",FACE,{"disambiguationData":[TD([makeQuery(id+"F13.opExtrude","SWEPT_FACE",FACE,{"disambiguationData":[OSD([sQuery(id+"F12.wireOp",EDGE,"E51.0")])]})])],"derivedFrom":makeQuery(id+"F5.boolean.opBoolean","MERGE",FACE,{"derivedFrom":[makeQuery(id+"F3.opExtrude","CAP_FACE",FACE,{"disambiguationData":[OSD([sQuery(id+"F2.wireOp",EDGE,"E10.top"),sQuery(id+"F2.wireOp",EDGE,"E10.left"),sQuery(id+"F2.wireOp",EDGE,"E10.right"),sQuery(id+"F2.wireOp",EDGE,"E12.top"),sQuery(id+"F2.wireOp",EDGE,"E12.left"),sQuery(id+"F2.wireOp",EDGE,"E12.right")])],"isStart":false}),makeQuery(id+"F3.opExtrude","CAP_FACE",FACE,{"disambiguationData":[OSD([sQuery(id+"F2.wireOp",EDGE,"E11.top"),sQuery(id+"F2.wireOp",EDGE,"E11.left"),sQuery(id+"F2.wireOp",EDGE,"E11.right"),sQuery(id+"F2.wireOp",EDGE,"E13.top"),sQuery(id+"F2.wireOp",EDGE,"E13.left"),sQuery(id+"F2.wireOp",EDGE,"E13.right")])],"isStart":false}),makeQuery(id+"F5.opExtrude","SWEPT_FACE",FACE,{"disambiguationData":[OSD([sQuery(id+"F4.wireOp",EDGE,"E14")])]})]})});
            extrude(context, id + "F16", {"entities" : qUnion([Q0]), "operationType" : NewBodyOperationType.REMOVE, "oppositeDirection" : true, "depth" : 1 * mm});
        }
        {
            var Q0;
            {var subQ7=sQuery(id+"F4.wireOp",EDGE,"E14");var subQ8=sQuery(id+"F2.wireOp",EDGE,"E12.top");var subQ9=sQuery(id+"F2.wireOp",EDGE,"E13.left");var subQ10=sQuery(id+"F2.wireOp",EDGE,"E11.left");var subQ11=sQuery(id+"F2.wireOp",EDGE,"E11.top");var subQ12=sQuery(id+"F2.wireOp",EDGE,"E13.top");var subQ13=sQuery(id+"F2.wireOp",EDGE,"E10.top");var subQ14=sQuery(id+"F2.wireOp",EDGE,"E12.left");var subQ15=sQuery(id+"F2.wireOp",EDGE,"E10.left");Q0=makeQuery(id+"F13.boolean.opBoolean","SPLIT",FACE,{"disambiguationData":[TD([makeQuery(id+"F1.opExtrude","SWEPT_FACE",FACE,{"disambiguationData":[OSD([sQuery(id+"F0.wireOp",EDGE,"E0.left")])]})])],"derivedFrom":makeQuery(id+"F5.boolean.opBoolean","MERGE",FACE,{"derivedFrom":[makeQuery(id+"F3.opExtrude","CAP_FACE",FACE,{"disambiguationData":[OSD([subQ13,subQ15,sQuery(id+"F2.wireOp",EDGE,"E10.right"),subQ8,subQ14,sQuery(id+"F2.wireOp",EDGE,"E12.right")])],"isStart":false}),makeQuery(id+"F3.opExtrude","CAP_FACE",FACE,{"disambiguationData":[OSD([subQ11,subQ10,sQuery(id+"F2.wireOp",EDGE,"E11.right"),subQ12,subQ9,sQuery(id+"F2.wireOp",EDGE,"E13.right")])],"isStart":false}),makeQuery(id+"F5.opExtrude","SWEPT_FACE",FACE,{"disambiguationData":[OSD([subQ7])]})]})});}
            var sketch = newSketch(context, id + "F17", { "sketchPlane" : qUnion([Q0])});
            skPoint(sketch, "E89.2", {"position": v(-78.15, 30) * mm});
            skPoint(sketch, "E89.3", {"position": v(-38.15, 30) * mm});
            skPoint(sketch, "E89.4", {"position": v(-38.15, 0) * mm});
            skPoint(sketch, "E89.5", {"position": v(-78.15, 0) * mm});
            skPoint(sketch, "E89.16", {"position": v(-65.15, 21) * mm});
            skPoint(sketch, "E89.18", {"position": v(-65.15, 9) * mm});
            skPoint(sketch, "E89.20", {"position": v(-53.65, 21) * mm});
            skPoint(sketch, "E89.22", {"position": v(-53.65, 9) * mm});
            skPoint(sketch, "E89.24", {"position": v(-51.15, 21) * mm});
            skPoint(sketch, "E89.26", {"position": v(-42.15, 21) * mm});
            skPoint(sketch, "E89.28", {"position": v(-62.65, 21) * mm});
            skPoint(sketch, "E89.30", {"position": v(-62.65, 9) * mm});
            skPoint(sketch, "E89.46", {"position": v(-67.15, 11) * mm});
            skPoint(sketch, "E89.48", {"position": v(-67.15, 19) * mm});
            skPoint(sketch, "E89.55", {"position": v(-42.15, 9) * mm});
            skPoint(sketch, "E89.57", {"position": v(-42.15, 12.5) * mm});
            skPoint(sketch, "E89.59", {"position": v(-44.15, 14.5) * mm});
            skPoint(sketch, "E89.61", {"position": v(-44.15, 19) * mm});
            skPoint(sketch, "E89.63", {"position": v(-49.15, 19) * mm});
            skPoint(sketch, "E89.70", {"position": v(-58.15, 30) * mm});
            skPoint(sketch, "E89.71", {"position": v(-58.15, 27) * mm});
            skLineSegment(sketch, "E89.72", {"start": v(-58.15, 30.5) * mm, "end": v(-64.15, 30.5) * mm});
            skLineSegment(sketch, "E89.73", {"start": v(-64.15, 30.5) * mm, "end": v(-58.15, 21.5) * mm});
            skLineSegment(sketch, "E89.74", {"start": v(-58.15, 30.5) * mm, "end": v(-52.15, 30.5) * mm});
            skLineSegment(sketch, "E89.75", {"start": v(-58.15, 21.5) * mm, "end": v(-52.15, 30.5) * mm});
            skPoint(sketch, "E90.orphan", {"position": v(-63.46, 29.46) * mm});
            skPoint(sketch, "E91.orphan", {"position": v(-78.15, 15) * mm});
            skPoint(sketch, "E89.45.end.orphan", {"position": v(-68.15, 11) * mm});
            skPoint(sketch, "E89.45.start.orphan", {"position": v(-74.15, 11) * mm});
            skPoint(sketch, "E89.6.end.orphan", {"position": v(-67.15, 21) * mm});
            skPoint(sketch, "E89.6.start.orphan", {"position": v(-74.15, 21) * mm});
            skPoint(sketch, "E89.68.start.orphan", {"position": v(-58.15, 11) * mm});
            skPoint(sketch, "E89.34.end.orphan", {"position": v(-55.65, 12) * mm});
            skPoint(sketch, "E89.34.start.orphan", {"position": v(-56.65, 11) * mm});
            skPoint(sketch, "E89.36.start.orphan", {"position": v(-55.65, 18) * mm});
            skPoint(sketch, "E89.37.end.orphan", {"position": v(-56.65, 19) * mm});
            skPoint(sketch, "E89.37.start.orphan", {"position": v(-55.65, 18) * mm});
            skPoint(sketch, "E89.32.start.orphan", {"position": v(-60.65, 19) * mm});
            skPoint(sketch, "E89.69.end.orphan", {"position": v(-58.15, 19) * mm});
            skPoint(sketch, "E89.69.start.orphan", {"position": v(-58.15, 21) * mm});
            skPoint(sketch, "E89.40.end.orphan", {"position": v(-68.15, 19) * mm});
            skPoint(sketch, "E89.40.start.orphan", {"position": v(-74.15, 19) * mm});
            skPoint(sketch, "E89.38.end.orphan", {"position": v(-74.15, 19) * mm});
            skPoint(sketch, "E89.38.start.orphan", {"position": v(-74.15, 21) * mm});
            skPoint(sketch, "E89.49.end.orphan", {"position": v(-68.15, 19) * mm});
            skPoint(sketch, "E89.49.start.orphan", {"position": v(-67.15, 18) * mm});
            skPoint(sketch, "E89.17.end.orphan", {"position": v(-67.15, 21) * mm});
            skPoint(sketch, "E89.17.start.orphan", {"position": v(-65.15, 19) * mm});
            skPoint(sketch, "E89.41.end.orphan", {"position": v(-67.15, 18) * mm});
            skPoint(sketch, "E89.41.start.orphan", {"position": v(-67.15, 16) * mm});
            skPoint(sketch, "E89.42.end.orphan", {"position": v(-67.15, 16) * mm});
            skPoint(sketch, "E89.42.start.orphan", {"position": v(-74.15, 16) * mm});
            skPoint(sketch, "E89.43.end.orphan", {"position": v(-67.15, 14) * mm});
            skPoint(sketch, "E89.43.start.orphan", {"position": v(-74.15, 14) * mm});
            skPoint(sketch, "E89.76.end.orphan", {"position": v(-74.15, 14) * mm});
            skPoint(sketch, "E89.44.end.orphan", {"position": v(-67.15, 12) * mm});
            skPoint(sketch, "E89.44.start.orphan", {"position": v(-67.15, 14) * mm});
            skPoint(sketch, "E89.47.end.orphan", {"position": v(-67.15, 12) * mm});
            skPoint(sketch, "E89.47.start.orphan", {"position": v(-68.15, 11) * mm});
            skPoint(sketch, "E89.39.end.orphan", {"position": v(-74.15, 11) * mm});
            skPoint(sketch, "E89.39.start.orphan", {"position": v(-74.15, 9) * mm});
            skPoint(sketch, "E89.7.end.orphan", {"position": v(-67.15, 9) * mm});
            skPoint(sketch, "E89.7.start.orphan", {"position": v(-74.15, 9) * mm});
            skPoint(sketch, "E89.19.end.orphan", {"position": v(-65.15, 11) * mm});
            skPoint(sketch, "E89.19.start.orphan", {"position": v(-67.15, 9) * mm});
            skPoint(sketch, "E89.8.end.orphan", {"position": v(-65.15, 11) * mm});
            skPoint(sketch, "E89.11.end.orphan", {"position": v(-62.65, 10) * mm});
            skPoint(sketch, "E89.35.end.orphan", {"position": v(-60.65, 11) * mm});
            skPoint(sketch, "E89.33.end.orphan", {"position": v(-56.65, 11) * mm});
            skPoint(sketch, "E89.10.end.orphan", {"position": v(-56.65, 9) * mm});
            skPoint(sketch, "E89.10.start.orphan", {"position": v(-61.65, 9) * mm});
            skPoint(sketch, "E89.23.end.orphan", {"position": v(-53.65, 12) * mm});
            skPoint(sketch, "E89.23.start.orphan", {"position": v(-56.65, 9) * mm});
            skPoint(sketch, "E89.12.start.orphan", {"position": v(-53.65, 18) * mm});
            skPoint(sketch, "E89.21.end.orphan", {"position": v(-56.65, 21) * mm});
            skPoint(sketch, "E89.21.start.orphan", {"position": v(-53.65, 18) * mm});
            skPoint(sketch, "E89.9.end.orphan", {"position": v(-56.65, 21) * mm});
            skPoint(sketch, "E89.29.end.orphan", {"position": v(-62.65, 20) * mm});
            skPoint(sketch, "E89.29.start.orphan", {"position": v(-61.65, 21) * mm});
            skPoint(sketch, "E89.31.end.orphan", {"position": v(-61.65, 9) * mm});
            skPoint(sketch, "E89.31.start.orphan", {"position": v(-62.65, 10) * mm});
            skPoint(sketch, "E89.50.end.orphan", {"position": v(-49.15, 9) * mm});
            skPoint(sketch, "E89.50.start.orphan", {"position": v(-51.15, 9) * mm});
            skPoint(sketch, "E89.14.start.orphan", {"position": v(-51.15, 19) * mm});
            skPoint(sketch, "E89.25.end.orphan", {"position": v(-51.15, 19) * mm});
            skPoint(sketch, "E89.25.start.orphan", {"position": v(-49.15, 21) * mm});
            skPoint(sketch, "E89.13.end.orphan", {"position": v(-44.15, 21) * mm});
            skPoint(sketch, "E89.13.start.orphan", {"position": v(-49.15, 21) * mm});
            skPoint(sketch, "E89.27.end.orphan", {"position": v(-44.15, 21) * mm});
            skPoint(sketch, "E89.27.start.orphan", {"position": v(-42.15, 19) * mm});
            skPoint(sketch, "E92.orphan", {"position": v(-58.15, 0) * mm});
            skPoint(sketch, "E89.1.end.orphan", {"position": v(-52.84, 29.46) * mm});
            skPoint(sketch, "E89.56.end.orphan", {"position": v(-45.15, 19) * mm});
            skPoint(sketch, "E89.56.start.orphan", {"position": v(-48.15, 19) * mm});
            skPoint(sketch, "E89.64.end.orphan", {"position": v(-49.15, 18) * mm});
            skPoint(sketch, "E89.64.start.orphan", {"position": v(-48.15, 19) * mm});
            skPoint(sketch, "E89.62.end.orphan", {"position": v(-45.15, 19) * mm});
            skPoint(sketch, "E89.62.start.orphan", {"position": v(-44.15, 18) * mm});
            skPoint(sketch, "E89.52.end.orphan", {"position": v(-44.15, 15.5) * mm});
            skPoint(sketch, "E89.52.start.orphan", {"position": v(-44.15, 18) * mm});
            skPoint(sketch, "E93.trimOffspring.end.orphan", {"position": v(-38.15, 15) * mm});
            skPoint(sketch, "E89.60.end.orphan", {"position": v(-44.15, 15.5) * mm});
            skPoint(sketch, "E89.53.end.orphan", {"position": v(-47.96, 14.5) * mm});
            skPoint(sketch, "E89.53.start.orphan", {"position": v(-45.15, 14.5) * mm});
            skPoint(sketch, "E89.51.start.orphan", {"position": v(-49.15, 9) * mm});
            skPoint(sketch, "E89.66.end.orphan", {"position": v(-48.76, 12.5) * mm});
            skPoint(sketch, "E89.66.start.orphan", {"position": v(-48.76, 14.5) * mm});
            skPoint(sketch, "E89.65.end.orphan", {"position": v(-48.76, 14.5) * mm});
            skPoint(sketch, "E89.65.start.orphan", {"position": v(-47.96, 14.5) * mm});
            skPoint(sketch, "E89.67.end.orphan", {"position": v(-47.88, 12.5) * mm});
            skPoint(sketch, "E89.67.start.orphan", {"position": v(-48.76, 12.5) * mm});
            skPoint(sketch, "E89.54.end.orphan", {"position": v(-44.15, 12.5) * mm});
            skPoint(sketch, "E89.54.start.orphan", {"position": v(-47.88, 12.5) * mm});
            skPoint(sketch, "E89.58.end.orphan", {"position": v(-42.15, 14.5) * mm});
            skPoint(sketch, "E89.58.start.orphan", {"position": v(-44.15, 12.5) * mm});
            skPoint(sketch, "E89.15.end.orphan", {"position": v(-42.15, 14.5) * mm});
            skSolve(sketch);
        }
        {
            var Q0;
            {var subQ6=sQuery(id+"F17.wireOp",EDGE,"E89.72");Q0=makeQuery(id+"F17.imprint","IMPRINT",FACE,{"disambiguationData":[TD([[makeQuery(id+"F17.imprint","IMPRINT",EDGE,{"derivedFrom":subQ6}),1.0]])]});}
            extrude(context, id + "F18", {"entities" : qUnion([Q0]), "operationType" : NewBodyOperationType.REMOVE, "oppositeDirection" : true, "depth" : 1.5 * mm});
        }
        {
            var Q0;
            Q0=makeQuery(id+"F5.boolean.opBoolean","MERGE",FACE,{"derivedFrom":[makeQuery(id+"F3.opExtrude","SWEPT_FACE",FACE,{"disambiguationData":[OSD([sQuery(id+"F2.wireOp",EDGE,"E12.top")])]}),makeQuery(id+"F3.opExtrude","SWEPT_FACE",FACE,{"disambiguationData":[OSD([sQuery(id+"F2.wireOp",EDGE,"E13.top")])]}),makeQuery(id+"F5.opExtrude","SWEPT_FACE",FACE,{"disambiguationData":[OSD([sQuery(id+"F4.wireOp",EDGE,"E15")])]})]});
            var sketch = newSketch(context, id + "F19", { "sketchPlane" : qUnion([Q0])});
            skLineSegment(sketch, "E94.0", {"start": v(52.22, -24) * mm, "end": v(64.07, -24) * mm});
            skLineSegment(sketch, "E95.MirrorCS", {"start": v(52.23, -18) * mm, "end": v(64.07, -18) * mm});
            skArc(sketch, "E96", {"start": v(52.23, -18) * mm, "mid": v(49.23, -21) * mm, "end": v(52.22, -24) * mm});
            skArc(sketch, "E97", {"start": v(64.07, -24) * mm, "mid": v(67.07, -21) * mm, "end": v(64.07, -18) * mm});
            skPoint(sketch, "E98.orphan", {"position": v(58.15, 0) * mm});
            skSolve(sketch);
        }
        {
            var Q0;
            Q0 = qSketchRegion(id + "F19", true);
            extrude(context, id + "F20", {"entities" : qUnion([Q0]), "operationType" : NewBodyOperationType.REMOVE, "oppositeDirection" : true, "depth" : 25 * mm});
        }
        {
            var Q0;
            Q0=makeQuery(id+"F3.opExtrude","CAP_EDGE",EDGE,{"disambiguationData":[OSD([sQuery(id+"F2.wireOp",EDGE,"E10.left"),sQuery(id+"F2.wireOp",EDGE,"E12.left")])],"isStart":false});
            var Q1;
            Q1=makeQuery(id+"F3.opExtrude","CAP_EDGE",EDGE,{"disambiguationData":[OSD([sQuery(id+"F2.wireOp",EDGE,"E11.left"),sQuery(id+"F2.wireOp",EDGE,"E13.left")])],"isStart":false});
            var Q2;
            Q2=makeQuery(id+"F5.boolean.opBoolean","MERGE",EDGE,{"derivedFrom":[makeQuery(id+"F3.opExtrude","CAP_EDGE",EDGE,{"disambiguationData":[OSD([sQuery(id+"F2.wireOp",EDGE,"E10.top")])],"isStart":false}),makeQuery(id+"F3.opExtrude","CAP_EDGE",EDGE,{"disambiguationData":[OSD([sQuery(id+"F2.wireOp",EDGE,"E11.top")])],"isStart":false}),makeQuery(id+"F5.opExtrude","SWEPT_EDGE",EDGE,{"disambiguationData":[OSD([sQuery(id+"F4.wireOp",EDGE,"E14"),sQuery(id+"F4.wireOp",EDGE,"E21")])]})]});
            chamfer(context, id + "F21", {"entities" : qUnion([Q0, Q1, Q2]), "width" : 2 * mm, "tangentPropagation" : true});
        }
        {
            var Q0;
            Q0=makeQuery(id+"F5.boolean.opBoolean","MERGE",FACE,{"derivedFrom":[makeQuery(id+"F1.opExtrude","CAP_FACE",FACE,{"disambiguationData":[OSD([sQuery(id+"F0.wireOp",EDGE,"E0.bottom"),sQuery(id+"F0.wireOp",EDGE,"E0.top"),sQuery(id+"F0.wireOp",EDGE,"E0.left"),sQuery(id+"F0.wireOp",EDGE,"E0.right"),sQuery(id+"F0.wireOp",EDGE,"E1"),sQuery(id+"F0.wireOp",EDGE,"E2"),sQuery(id+"F0.wireOp",EDGE,"E3"),sQuery(id+"F0.wireOp",EDGE,"E4")])],"isStart":true}),makeQuery(id+"F5.opExtrude","SWEPT_FACE",FACE,{"disambiguationData":[OSD([sQuery(id+"F4.wireOp",EDGE,"E16")])]})]});
            var sketch = newSketch(context, id + "F22", { "sketchPlane" : qUnion([Q0])});
            skCircle(sketch, "E99.0", {"center": v(9, 5) * mm, "radius": 2.8 * mm});
            skLineSegment(sketch, "E99.1", {"start": v(11.33, 7.24) * mm, "end": v(8.23, 8.14) * mm});
            skLineSegment(sketch, "E99.2", {"start": v(8.23, 8.14) * mm, "end": v(5.9, 5.9) * mm});
            skLineSegment(sketch, "E99.3", {"start": v(5.9, 5.9) * mm, "end": v(6.67, 2.76) * mm});
            skLineSegment(sketch, "E99.4", {"start": v(6.67, 2.76) * mm, "end": v(9.77, 1.86) * mm});
            skLineSegment(sketch, "E99.5", {"start": v(9.77, 1.86) * mm, "end": v(12.1, 4.1) * mm});
            skLineSegment(sketch, "E99.6", {"start": v(12.1, 4.1) * mm, "end": v(11.33, 7.24) * mm});
            skPoint(sketch, "E99.7", {"position": v(9.78, 7.69) * mm});
            skSolve(sketch);
        }
        {
            var Q0;
            Q0 = qSketchRegion(id + "F22", true);
            extrude(context, id + "F23", {"entities" : qUnion([Q0]), "operationType" : NewBodyOperationType.REMOVE, "oppositeDirection" : true, "depth" : 2.5 * mm});
        }
        {
            var Q0;
            {var subQ7=sQuery(id+"F4.wireOp",EDGE,"E14");var subQ8=sQuery(id+"F2.wireOp",EDGE,"E12.top");var subQ9=sQuery(id+"F2.wireOp",EDGE,"E13.left");var subQ10=sQuery(id+"F2.wireOp",EDGE,"E11.left");var subQ11=sQuery(id+"F2.wireOp",EDGE,"E11.top");var subQ12=sQuery(id+"F2.wireOp",EDGE,"E13.top");var subQ13=sQuery(id+"F2.wireOp",EDGE,"E10.top");var subQ14=sQuery(id+"F2.wireOp",EDGE,"E12.left");var subQ15=sQuery(id+"F2.wireOp",EDGE,"E10.left");Q0=makeQuery(id+"F13.boolean.opBoolean","SPLIT",FACE,{"disambiguationData":[TD([makeQuery(id+"F1.opExtrude","SWEPT_FACE",FACE,{"disambiguationData":[OSD([sQuery(id+"F0.wireOp",EDGE,"E0.left")])]})])],"derivedFrom":makeQuery(id+"F5.boolean.opBoolean","MERGE",FACE,{"derivedFrom":[makeQuery(id+"F3.opExtrude","CAP_FACE",FACE,{"disambiguationData":[OSD([subQ13,subQ15,sQuery(id+"F2.wireOp",EDGE,"E10.right"),subQ8,subQ14,sQuery(id+"F2.wireOp",EDGE,"E12.right")])],"isStart":false}),makeQuery(id+"F3.opExtrude","CAP_FACE",FACE,{"disambiguationData":[OSD([subQ11,subQ10,sQuery(id+"F2.wireOp",EDGE,"E11.right"),subQ12,subQ9,sQuery(id+"F2.wireOp",EDGE,"E13.right")])],"isStart":false}),makeQuery(id+"F5.opExtrude","SWEPT_FACE",FACE,{"disambiguationData":[OSD([subQ7])]})]})});}
            var sketch = newSketch(context, id + "F24", { "sketchPlane" : qUnion([Q0])});
            skCircle(sketch, "E100.4", {"center": v(-18, 61.5) * mm, "radius": 1.7 * mm});
            skCircle(sketch, "E100.5", {"center": v(-103.3, 61.5) * mm, "radius": 1.7 * mm});
            skCircle(sketch, "E100.7", {"center": v(-9, 5) * mm, "radius": 2.2 * mm});
            skPoint(sketch, "E100.0.start.orphan", {"position": v(0, 0) * mm});
            skPoint(sketch, "E100.2.start.orphan", {"position": v(0, 0) * mm});
            skSolve(sketch);
        }
        {
            var Q0;
            Q0 = qSketchRegion(id + "F24", true);
            extrude(context, id + "F25", {"entities" : qUnion([Q0]), "operationType" : NewBodyOperationType.REMOVE, "oppositeDirection" : true, "depth" : 25 * mm});
        }
        {
            var Q0;
            Q0=makeQuery(id+"F5.boolean.opBoolean","MERGE",FACE,{"derivedFrom":[makeQuery(id+"F3.boolean.opBoolean","MERGE",FACE,{"derivedFrom":[makeQuery(id+"F1.opExtrude","SWEPT_FACE",FACE,{"disambiguationData":[OSD([sQuery(id+"F0.wireOp",EDGE,"E0.right")])]}),makeQuery(id+"F3.opExtrude","SWEPT_FACE",FACE,{"disambiguationData":[OSD([sQuery(id+"F2.wireOp",EDGE,"E10.left"),sQuery(id+"F2.wireOp",EDGE,"E12.left")])]})]}),makeQuery(id+"F5.opExtrude","CAP_FACE",FACE,{"disambiguationData":[OSD([sQuery(id+"F4.wireOp",EDGE,"E14"),sQuery(id+"F4.wireOp",EDGE,"E15"),sQuery(id+"F4.wireOp",EDGE,"E16"),sQuery(id+"F4.wireOp",EDGE,"E17"),sQuery(id+"F4.wireOp",EDGE,"E18"),sQuery(id+"F4.wireOp",EDGE,"E19"),sQuery(id+"F4.wireOp",EDGE,"E20"),sQuery(id+"F4.wireOp",EDGE,"E21")])],"isStart":false})]});
            var sketch = newSketch(context, id + "F26", { "sketchPlane" : qUnion([Q0])});
            skCircle(sketch, "E101", {"center": v(5.3, -15.7) * mm, "radius": 4 * mm});
            skSolve(sketch);
        }
        {
            var Q0;
            Q0 = qSketchRegion(id + "F26", true);
            extrude(context, id + "F27", {"entities" : qUnion([Q0]), "operationType" : NewBodyOperationType.REMOVE, "oppositeDirection" : true, "depth" : 8 * mm});
        }
    });
